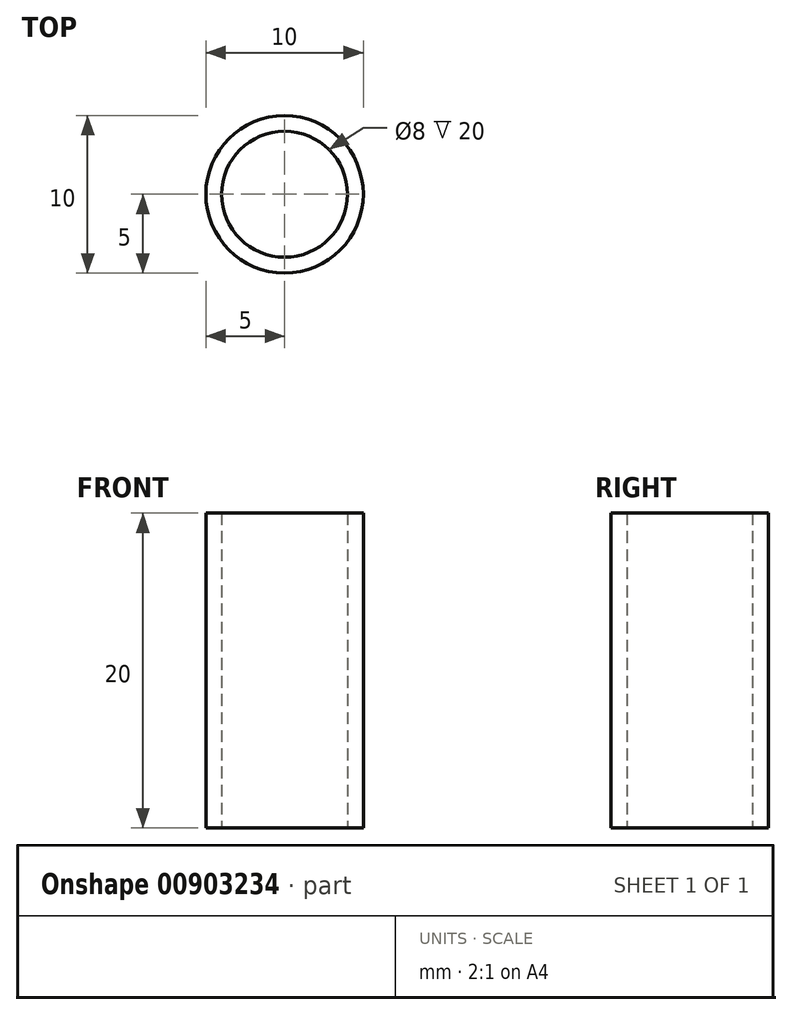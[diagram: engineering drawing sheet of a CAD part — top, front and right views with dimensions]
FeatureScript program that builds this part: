
annotation { "Feature Type Name" : "Feature", "Feature Type Description" : "" }
export const myFeature = defineFeature(function(context is Context, id is Id, definition is map)
    precondition{}
    {
        {
            var Q0;
            Q0=qCreatedBy(makeId("Top.planeOp"),FACE);
            var sketch = newSketch(context, id + "F0", { "sketchPlane" : qUnion([Q0])});
            skCircle(sketch, "E0", {"center": v(0, 0) * mm, "radius": 5 * mm});
            skSolve(sketch);
        }
        {
            var Q0;
            Q0 = qSketchRegion(id + "F0", true);
            extrude(context, id + "F1", {"entities" : qUnion([Q0]), "depth" : 20 * mm, "offsetDistance" : 25.4 * mm});
        }
        {
            var Q0;
            Q0=qCreatedBy(makeId("Top.planeOp"),FACE);
            var sketch = newSketch(context, id + "F2", { "sketchPlane" : qUnion([Q0])});
            skCircle(sketch, "E1", {"center": v(0, 0) * mm, "radius": 4 * mm});
            skSolve(sketch);
        }
        {
            var Q0;
            Q0 = qSketchRegion(id + "F2", true);
            extrude(context, id + "F3", {"entities" : qUnion([Q0]), "operationType" : NewBodyOperationType.REMOVE, "oppositeDirection" : true, "depth" : -20 * mm, "offsetDistance" : 25 * mm});
        }
    });
